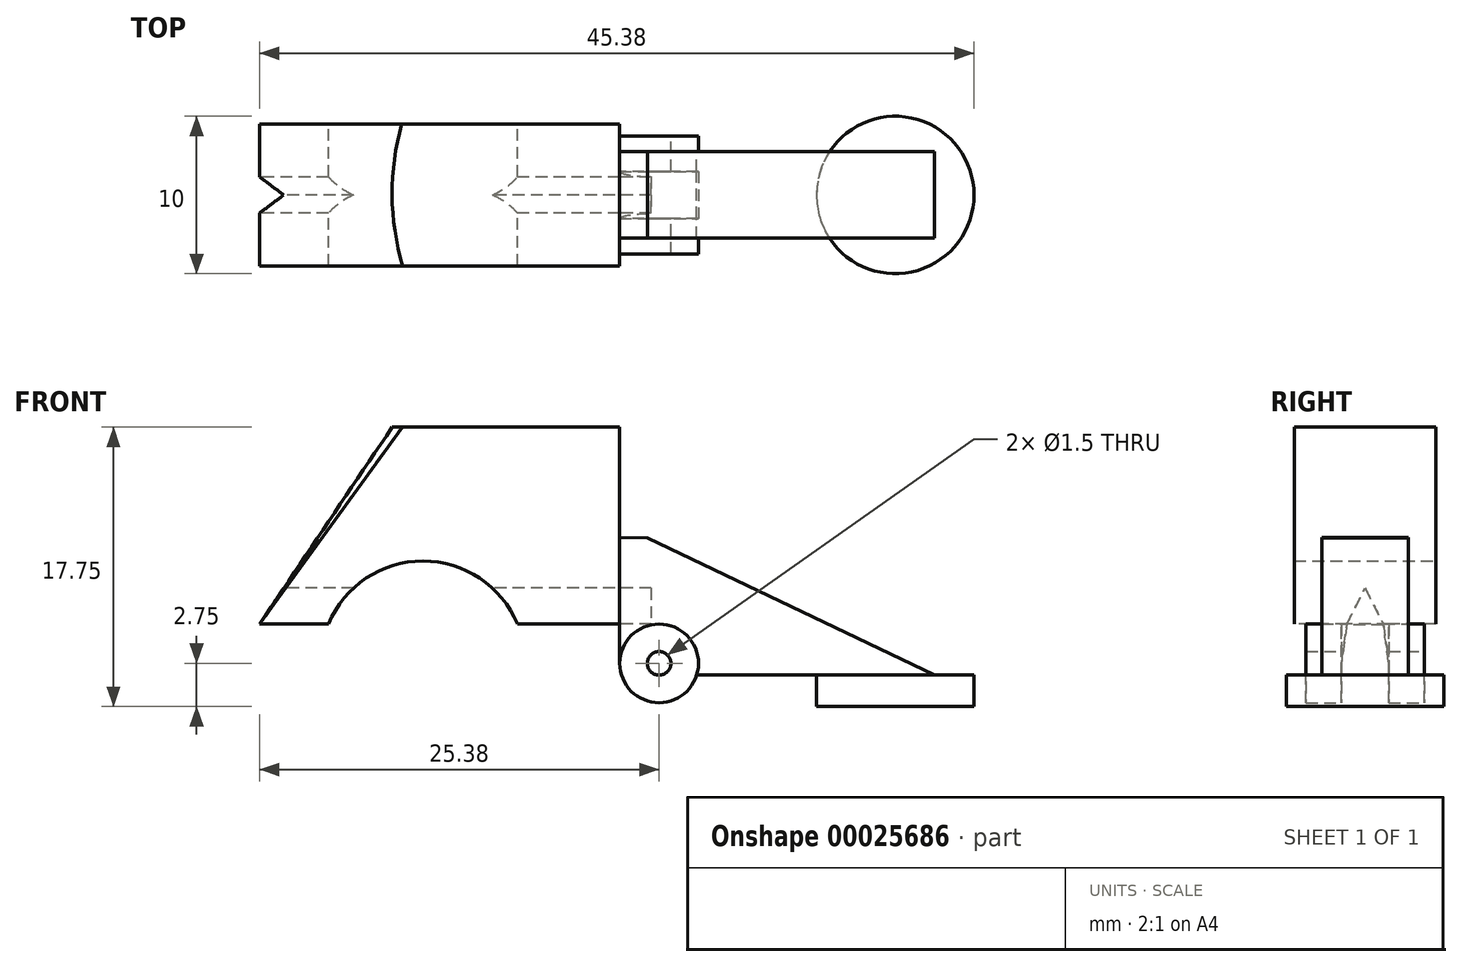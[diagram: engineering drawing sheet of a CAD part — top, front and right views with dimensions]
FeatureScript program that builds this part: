
annotation { "Feature Type Name" : "Feature", "Feature Type Description" : "" }
export const myFeature = defineFeature(function(context is Context, id is Id, definition is map)
    precondition{}
    {
        {
            var Q0;
            Q0=qCreatedBy(makeId("Front.planeOp"),FACE);
            var sketch = newSketch(context, id + "F0", { "sketchPlane" : qUnion([Q0])});
            skCircle(sketch, "E0", {"center": v(0, 0) * mm, "radius": 2.5 * mm});
            skCircle(sketch, "E1", {"center": v(0, 0) * mm, "radius": 0.75 * mm});
            skSolve(sketch);
        }
        {
            var Q0;
            Q0 = qSketchRegion(id + "F0", true);
            extrude(context, id + "F1", {"entities" : qUnion([Q0]), "depth" : 3.75 * mm, "hasSecondDirection" : true, "secondDirectionOppositeDirection" : true, "secondDirectionDepth" : 3.75 * mm});
        }
        {
            var Q0;
            Q0=qCreatedBy(makeId("Front.planeOp"),FACE);
            var sketch = newSketch(context, id + "F2", { "sketchPlane" : qUnion([Q0])});
            skLineSegment(sketch, "E2", {"start": v(0, -0.75) * mm, "end": v(17.5, -0.75) * mm});
            skLineSegment(sketch, "E3", {"start": v(-2.5, 0) * mm, "end": v(-2.5, 8) * mm});
            skLineSegment(sketch, "E4", {"start": v(-0.75, 0) * mm, "end": v(-0.75, 7.97) * mm});
            skLineSegment(sketch, "E5", {"start": v(-0.75, 7.97) * mm, "end": v(17.5, -0.75) * mm});
            skLineSegment(sketch, "E6", {"start": v(-0.75, 7.97) * mm, "end": v(-2.5, 8) * mm});
            skLineSegment(sketch, "E7", {"start": v(-2.5, 0) * mm, "end": v(-0.75, 2.38) * mm});
            skLineSegment(sketch, "E8", {"start": v(-0.75, 2.38) * mm, "end": v(2.38, -0.75) * mm});
            skSolve(sketch);
        }
        {
            var Q0;
            Q0 = qSketchRegion(id + "F2", true);
            extrude(context, id + "F3", {"entities" : qUnion([Q0]), "operationType" : NewBodyOperationType.ADD, "depth" : 2.75 * mm, "hasSecondDirection" : true, "secondDirectionOppositeDirection" : true, "secondDirectionDepth" : 2.75 * mm});
        }
        {
            var Q0;
            Q0=makeQuery(id+"F3.opExtrude","SWEPT_FACE",FACE,{"disambiguationData":[OSD([sQuery(id+"F2.wireOp",EDGE,"E2")])]});
            var sketch = newSketch(context, id + "F4", { "sketchPlane" : qUnion([Q0])});
            skLineSegment(sketch, "E9", {"start": v(0, 0) * mm, "end": v(15, 0) * mm});
            skCircle(sketch, "E10", {"center": v(15, 0) * mm, "radius": 5 * mm});
            skSolve(sketch);
        }
        {
            var Q0;
            Q0 = qSketchRegion(id + "F4", true);
            extrude(context, id + "F5", {"entities" : qUnion([Q0]), "operationType" : NewBodyOperationType.ADD, "depth" : 2 * mm});
        }
        {
            var Q0;
            Q0=qCreatedBy(makeId("Front.planeOp"),FACE);
            var sketch = newSketch(context, id + "F6", { "sketchPlane" : qUnion([Q0])});
            skLineSegment(sketch, "E11", {"start": v(-2.5, 15) * mm, "end": v(-17, 15) * mm});
            skLineSegment(sketch, "E12", {"start": v(-2.5, 2.5) * mm, "end": v(-25.5, 2.5) * mm});
            skLineSegment(sketch, "E13", {"start": v(-2.5, 15) * mm, "end": v(-2.5, 2.5) * mm});
            skLineSegment(sketch, "E14", {"start": v(-17, 15) * mm, "end": v(-25.5, 2.5) * mm});
            skSolve(sketch);
        }
        {
            var Q0;
            Q0 = qSketchRegion(id + "F6", true);
            extrude(context, id + "F7", {"entities" : qUnion([Q0]), "operationType" : NewBodyOperationType.ADD, "depth" : 4.5 * mm, "hasSecondDirection" : true, "secondDirectionOppositeDirection" : true, "secondDirectionDepth" : 4.5 * mm});
        }
        {
            var Q0;
            Q0=makeQuery(id+"F7.opExtrude","SWEPT_FACE",FACE,{"disambiguationData":[OSD([sQuery(id+"F6.wireOp",EDGE,"E11")])]});
            var sketch = newSketch(context, id + "F8", { "sketchPlane" : qUnion([Q0])});
            skLineSegment(sketch, "E15", {"start": v(-17, 4.5) * mm, "end": v(-16.34, 4.5) * mm});
            skLineSegment(sketch, "E16", {"start": v(-17, -4.5) * mm, "end": v(-16.28, -4.5) * mm});
            skLineSegment(sketch, "E17", {"start": v(-17, -4.5) * mm, "end": v(-17, 4.5) * mm});
            skArc(sketch, "E18", {"start": v(-16.34, 4.5) * mm, "mid": v(-16.96, 0) * mm, "end": v(-16.28, -4.5) * mm});
            skSolve(sketch);
        }
        {
            var Q0;
            {var subQ0=sQuery(id+"F6.wireOp",EDGE,"E12");var subQ2=sQuery(id+"F6.wireOp",EDGE,"E14");var subQ3=makeQuery(id+"F7.opExtrude","SWEPT_FACE",FACE,{"disambiguationData":[OSD([subQ2])]});Q0=makeQuery(id+"F16.boolean.opBoolean","SPLIT",FACE,{"disambiguationData":[TD([subQ3])],"derivedFrom":makeQuery(id+"F14.boolean.opBoolean","SPLIT",FACE,{"disambiguationData":[TD([makeQuery(id+"F14.opExtrude","SWEPT_FACE",FACE,{"disambiguationData":[OSD([sQuery(id+"F13.wireOp",EDGE,"E31")])]})])],"derivedFrom":makeQuery(id+"F7.opExtrude","SWEPT_FACE",FACE,{"disambiguationData":[OSD([subQ0])]})})});}
            var sketch = newSketch(context, id + "F9", { "sketchPlane" : qUnion([Q0])});
            skPoint(sketch, "E19.0", {"position": v(-25.5, -4.5) * mm});
            skLineSegment(sketch, "E20.bottom", {"start": v(-25.5, -4.5) * mm, "end": v(-25.38, -4.5) * mm});
            skLineSegment(sketch, "E20.top", {"start": v(-25.5, 4.5) * mm, "end": v(-25.38, 4.5) * mm});
            skLineSegment(sketch, "E20.left", {"start": v(-25.5, -4.5) * mm, "end": v(-25.5, 4.5) * mm});
            skLineSegment(sketch, "E20.right", {"start": v(-25.38, -4.5) * mm, "end": v(-25.38, 4.5) * mm});
            skSolve(sketch);
        }
        {
            var Q0;
            Q0=qCreatedBy(makeId("Front.planeOp"),FACE);
            var sketch = newSketch(context, id + "F10", { "sketchPlane" : qUnion([Q0])});
            skCircle(sketch, "E21", {"center": v(0, 0) * mm, "radius": 2.5 * mm});
            skSolve(sketch);
        }
        {
            var Q0;
            Q0 = qSketchRegion(id + "F10", true);
            extrude(context, id + "F11", {"entities" : qUnion([Q0]), "operationType" : NewBodyOperationType.REMOVE, "oppositeDirection" : true, "depth" : 1.5 * mm, "hasSecondDirection" : true, "secondDirectionOppositeDirection" : false, "secondDirectionDepth" : 1.5 * mm});
        }
        {
            var Q0;
            Q0=makeQuery(id+"F7.opExtrude","SWEPT_FACE",FACE,{"disambiguationData":[OSD([sQuery(id+"F6.wireOp",EDGE,"E14")])]});
            var sketch = newSketch(context, id + "F12", { "sketchPlane" : qUnion([Q0])});
            skLineSegment(sketch, "E22", {"start": v(-1.15, -12.27) * mm, "end": v(0, -9.52) * mm});
            skLineSegment(sketch, "E23", {"start": v(0, -9.52) * mm, "end": v(1.15, -12.27) * mm});
            skLineSegment(sketch, "E24", {"start": v(-1.15, -12.27) * mm, "end": v(1.15, -12.27) * mm});
            skSolve(sketch);
        }
        {
            var Q0;
            Q0=makeQuery(id+"F3.opExtrude","SWEPT_FACE",FACE,{"disambiguationData":[OSD([sQuery(id+"F2.wireOp",EDGE,"E3")])]});
            var sketch = newSketch(context, id + "F13", { "sketchPlane" : qUnion([Q0])});
            skPoint(sketch, "E25.0", {"position": v(0, 4.77) * mm});
            skPoint(sketch, "E26.0", {"position": v(-1.15, 2.5) * mm});
            skPoint(sketch, "E27.0", {"position": v(1.15, 2.5) * mm});
            skPoint(sketch, "E28.0", {"position": v(-1.5, 0) * mm});
            skPoint(sketch, "E29.0", {"position": v(1.5, 0) * mm});
            skLineSegment(sketch, "E30", {"start": v(-1.5, 0) * mm, "end": v(1.5, 0) * mm});
            skLineSegment(sketch, "E31", {"start": v(1.15, 2.5) * mm, "end": v(1.5, 0) * mm});
            skLineSegment(sketch, "E32", {"start": v(1.15, 2.5) * mm, "end": v(0, 4.77) * mm});
            skLineSegment(sketch, "E33", {"start": v(0, 4.77) * mm, "end": v(-1.15, 2.5) * mm});
            skLineSegment(sketch, "E34", {"start": v(-1.15, 2.5) * mm, "end": v(-1.5, 0) * mm});
            skSolve(sketch);
        }
        {
            var Q0;
            Q0 = qSketchRegion(id + "F13", true);
            extrude(context, id + "F14", {"entities" : qUnion([Q0]), "operationType" : NewBodyOperationType.REMOVE, "oppositeDirection" : true, "depth" : 2 * mm, "hasSecondDirection" : true, "secondDirectionBound" : SecondDirectionBoundingType.THROUGH_ALL, "secondDirectionOppositeDirection" : false, "secondDirectionDepth" : 25 * mm});
        }
        {
            var Q0;
            Q0=qCreatedBy(makeId("Front.planeOp"),FACE);
            var sketch = newSketch(context, id + "F15", { "sketchPlane" : qUnion([Q0])});
            skLineSegment(sketch, "E35", {"start": v(0, 0) * mm, "end": v(-15, 0) * mm});
            skCircle(sketch, "E36", {"center": v(-15, 0) * mm, "radius": 6.5 * mm});
            skSolve(sketch);
        }
        {
            var Q0;
            Q0 = qSketchRegion(id + "F15", true);
            extrude(context, id + "F16", {"entities" : qUnion([Q0]), "operationType" : NewBodyOperationType.REMOVE, "endBound" : BoundingType.THROUGH_ALL, "depth" : 25 * mm, "hasSecondDirection" : true, "secondDirectionBound" : SecondDirectionBoundingType.THROUGH_ALL, "secondDirectionOppositeDirection" : true, "secondDirectionDepth" : 25 * mm});
        }
        {
            var Q1;
            Q1 = qSketchRegion(id + "F9", true);
            var Q2;
            Q2 = qSketchRegion(id + "F8", true);
            loft(context, id + "F17", {"operationType" : NewBodyOperationType.REMOVE, "sheetProfilesArray" : [{ "sheetProfileEntities" : qUnion([Q1]) }, { "sheetProfileEntities" : qUnion([Q2]) }]});
        }
    });
